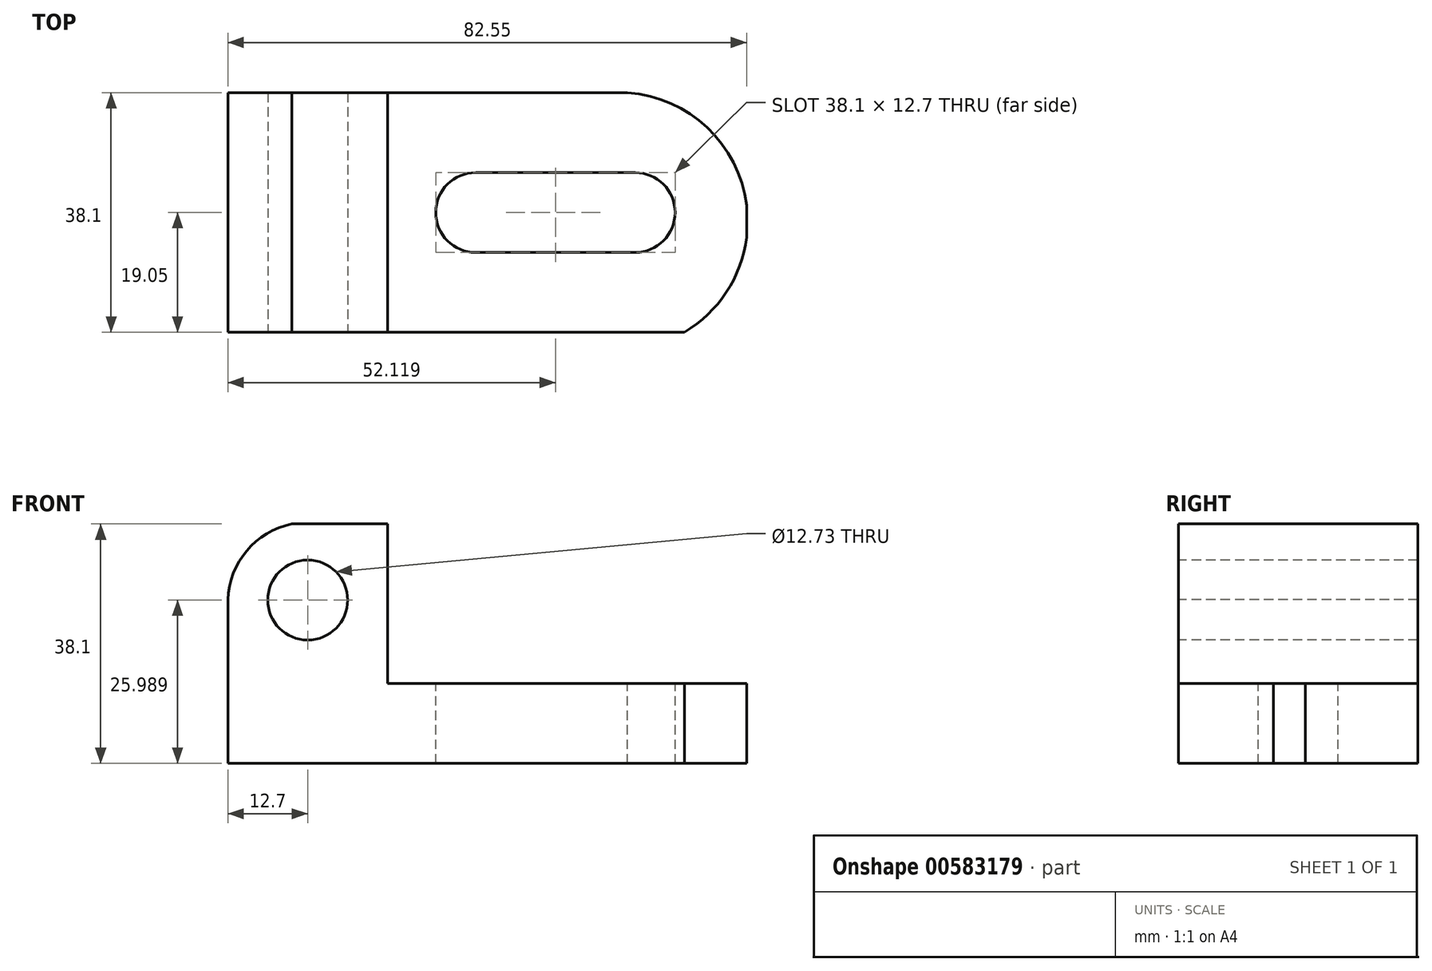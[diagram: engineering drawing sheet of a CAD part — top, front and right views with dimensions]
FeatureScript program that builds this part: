
annotation { "Feature Type Name" : "Feature", "Feature Type Description" : "" }
export const myFeature = defineFeature(function(context is Context, id is Id, definition is map)
    precondition{}
    {
        {
            var Q0;
            Q0=qCreatedBy(makeId("Front.planeOp"),FACE);
            var sketch = newSketch(context, id + "F0", { "sketchPlane" : qUnion([Q0])});
            skLineSegment(sketch, "E0.bottom", {"start": v(0, 0) * mm, "end": v(-82.55, 0) * mm});
            skLineSegment(sketch, "E0.top", {"start": v(0, 38.1) * mm, "end": v(-82.55, 38.1) * mm});
            skLineSegment(sketch, "E0.left", {"start": v(0, 0) * mm, "end": v(0, 38.1) * mm});
            skLineSegment(sketch, "E0.right", {"start": v(-82.55, 0) * mm, "end": v(-82.55, 38.1) * mm});
            skSolve(sketch);
        }
        {
            var Q0;
            Q0=makeQuery(id+"F0.imprint","IMPRINT",FACE,{"disambiguationData":[TD([[makeQuery(id+"F0.imprint","IMPRINT",EDGE,{"derivedFrom":sQuery(id+"F0.wireOp",EDGE,"E0.bottom")}),-1.0]])]});
            extrude(context, id + "F1", {"entities" : qUnion([Q0]), "depth" : 38.1 * mm, "offsetDistance" : 25.4 * mm});
        }
        {
            var Q0;
            Q0=makeQuery(id+"F1.opExtrude","CAP_FACE",FACE,{"disambiguationData":[OSD([sQuery(id+"F0.wireOp",EDGE,"E0.bottom"),sQuery(id+"F0.wireOp",EDGE,"E0.top"),sQuery(id+"F0.wireOp",EDGE,"E0.left"),sQuery(id+"F0.wireOp",EDGE,"E0.right")])],"isStart":false});
            var sketch = newSketch(context, id + "F2", { "sketchPlane" : qUnion([Q0])});
            skLineSegment(sketch, "E1", {"start": v(-57.15, 0) * mm, "end": v(-57.15, 12.7) * mm});
            skLineSegment(sketch, "E2", {"start": v(-57.15, 12.7) * mm, "end": v(-82.55, 12.7) * mm});
            skLineSegment(sketch, "E3", {"start": v(-57.15, 12.7) * mm, "end": v(-57.15, 38.1) * mm});
            skLineSegment(sketch, "E4", {"start": v(-57.15, 12.7) * mm, "end": v(0, 12.7) * mm});
            skSolve(sketch);
        }
        {
            var Q0;
            {var subQ0=sQuery(id+"F2.wireOp",EDGE,"E3");Q0=makeQuery(id+"F2.imprint","IMPRINT",FACE,{"disambiguationData":[TD([[makeQuery(id+"F2.imprint","IMPRINT",EDGE,{"derivedFrom":subQ0}),-1.0]])]});}
            extrude(context, id + "F3", {"entities" : qUnion([Q0]), "operationType" : NewBodyOperationType.REMOVE, "endBound" : BoundingType.THROUGH_ALL, "oppositeDirection" : true, "depth" : 25.4 * mm, "offsetDistance" : 25.4 * mm});
        }
        {
            var Q0;
            Q0=makeQuery(id+"F1.opExtrude","CAP_FACE",FACE,{"disambiguationData":[OSD([sQuery(id+"F0.wireOp",EDGE,"E0.bottom"),sQuery(id+"F0.wireOp",EDGE,"E0.top"),sQuery(id+"F0.wireOp",EDGE,"E0.left"),sQuery(id+"F0.wireOp",EDGE,"E0.right")])],"isStart":false});
            var sketch = newSketch(context, id + "F4", { "sketchPlane" : qUnion([Q0])});
            skCircle(sketch, "E5", {"center": v(-69.85, 25.99) * mm, "radius": 6.36 * mm});
            skSolve(sketch);
        }
        {
            var Q0;
            Q0=makeQuery(id+"F4.imprint","IMPRINT",FACE,{"disambiguationData":[TD([[makeQuery(id+"F4.imprint","IMPRINT",EDGE,{"derivedFrom":sQuery(id+"F4.wireOp",EDGE,"E5")}),1.0]])]});
            extrude(context, id + "F5", {"entities" : qUnion([Q0]), "operationType" : NewBodyOperationType.REMOVE, "endBound" : BoundingType.THROUGH_ALL, "oppositeDirection" : true, "depth" : 25.4 * mm, "offsetDistance" : 25.4 * mm});
        }
        {
            var Q0;
            Q0=makeQuery(id+"F3.boolean.opBoolean","COPY",FACE,{"derivedFrom":makeQuery(id+"F3.opExtrude","SWEPT_FACE",FACE,{"disambiguationData":[OSD([sQuery(id+"F2.wireOp",EDGE,"E4")])]})});
            var sketch = newSketch(context, id + "F6", { "sketchPlane" : qUnion([Q0])});
            skCircle(sketch, "E6", {"center": v(-43.13, -19.05) * mm, "radius": 6.35 * mm});
            skCircle(sketch, "E7", {"center": v(-17.73, -19.05) * mm, "radius": 6.35 * mm});
            skLineSegment(sketch, "E8", {"start": v(-43.13, -12.7) * mm, "end": v(-17.73, -12.7) * mm});
            skLineSegment(sketch, "E9", {"start": v(-43.13, -25.4) * mm, "end": v(-17.73, -25.4) * mm});
            skSolve(sketch);
        }
        {
            var Q0;
            {var subQ0=sQuery(id+"F6.wireOp",EDGE,"E8");Q0=makeQuery(id+"F6.imprint","IMPRINT",FACE,{"disambiguationData":[TD([[makeQuery(id+"F6.imprint","IMPRINT",EDGE,{"derivedFrom":subQ0}),-1.0]])]});}
            var Q1;
            {var subQ0=sQuery(id+"F6.wireOp",EDGE,"E6");var subQ1=makeQuery(id+"F6.imprint","INTERSECT",VERTEX,{"derivedFrom":[subQ0,sQuery(id+"F6.wireOp",EDGE,"E8")]});Q1=makeQuery(id+"F6.imprint","IMPRINT",FACE,{"disambiguationData":[TD([[makeQuery(id+"F6.imprint","IMPRINT",EDGE,{"disambiguationData":[TD([[subQ1,-1.0]])],"derivedFrom":subQ0}),1.0]])]});}
            var Q2;
            {var subQ0=sQuery(id+"F6.wireOp",EDGE,"E7");var subQ1=makeQuery(id+"F6.imprint","INTERSECT",VERTEX,{"derivedFrom":[subQ0,sQuery(id+"F6.wireOp",EDGE,"E8")]});Q2=makeQuery(id+"F6.imprint","IMPRINT",FACE,{"disambiguationData":[TD([[makeQuery(id+"F6.imprint","IMPRINT",EDGE,{"disambiguationData":[TD([[subQ1,-1.0]])],"derivedFrom":subQ0}),1.0]])]});}
            extrude(context, id + "F7", {"entities" : qUnion([Q0, Q1, Q2]), "operationType" : NewBodyOperationType.REMOVE, "oppositeDirection" : true, "depth" : 25.4 * mm, "offsetDistance" : 25.4 * mm});
        }
        {
            var Q0;
            Q0=makeQuery(id+"F1.opExtrude","CAP_FACE",FACE,{"disambiguationData":[OSD([sQuery(id+"F0.wireOp",EDGE,"E0.bottom"),sQuery(id+"F0.wireOp",EDGE,"E0.top"),sQuery(id+"F0.wireOp",EDGE,"E0.left"),sQuery(id+"F0.wireOp",EDGE,"E0.right")])],"isStart":false});
            var sketch = newSketch(context, id + "F8", { "sketchPlane" : qUnion([Q0])});
            skArc(sketch, "E10", {"start": v(-57.15, 25.4) * mm, "mid": v(-69.53, 38.35) * mm, "end": v(-82.55, 26.03) * mm});
            skSolve(sketch);
        }
        {
            var Q0;
            {var subQ0=sQuery(id+"F8.wireOp",EDGE,"E10");var subQ1=makeQuery(id+"F3.boolean.opBoolean","COPY",EDGE,{"derivedFrom":makeQuery(id+"F3.opExtrude","CAP_EDGE",EDGE,{"disambiguationData":[OSD([sQuery(id+"F2.wireOp",EDGE,"E3")])],"isStart":true})});var subQ2=makeQuery(id+"F8.imprint","INTERSECT",VERTEX,{"disambiguationData":[OD(1.0)],"derivedFrom":[subQ1,subQ0]});Q0=makeQuery(id+"F8.imprint","IMPRINT",FACE,{"disambiguationData":[TD([[makeQuery(id+"F8.imprint","IMPRINT",EDGE,{"disambiguationData":[TD([[subQ2,-1.0]])],"derivedFrom":subQ0}),-1.0]])]});}
            var Q1;
            {var subQ0=sQuery(id+"F8.wireOp",EDGE,"E10");var subQ1=makeQuery(id+"F1.opExtrude","CAP_EDGE",EDGE,{"disambiguationData":[OSD([sQuery(id+"F0.wireOp",EDGE,"E0.right")])],"isStart":false});var subQ2=makeQuery(id+"F8.imprint","INTERSECT",VERTEX,{"derivedFrom":[subQ1,subQ0]});Q1=makeQuery(id+"F8.imprint","IMPRINT",FACE,{"disambiguationData":[TD([[makeQuery(id+"F8.imprint","IMPRINT",EDGE,{"disambiguationData":[TD([[subQ2,1.0]])],"derivedFrom":subQ0}),-1.0]])]});}
            extrude(context, id + "F9", {"entities" : qUnion([Q0, Q1]), "operationType" : NewBodyOperationType.ADD, "depth" : 25.4 * mm, "offsetDistance" : 25.4 * mm});
        }
        {
            var Q0;
            Q0=makeQuery(id+"F9.opExtrude","CAP_FACE",FACE,{"disambiguationData":[OSD([sQuery(id+"F0.wireOp",EDGE,"E0.top"),sQuery(id+"F2.wireOp",EDGE,"E3"),sQuery(id+"F8.wireOp",EDGE,"E10")])],"isStart":false});
            var Q1;
            Q1=makeQuery(id+"F9.opExtrude","CAP_FACE",FACE,{"disambiguationData":[OSD([sQuery(id+"F0.wireOp",EDGE,"E0.top"),sQuery(id+"F0.wireOp",EDGE,"E0.right"),sQuery(id+"F8.wireOp",EDGE,"E10")])],"isStart":false});
            extrude(context, id + "F10", {"entities" : qUnion([Q0, Q1]), "operationType" : NewBodyOperationType.REMOVE, "endBound" : BoundingType.THROUGH_ALL, "oppositeDirection" : true, "depth" : 25.4 * mm, "offsetDistance" : 25.4 * mm});
        }
        {
            var Q0;
            Q0=makeQuery(id+"F3.boolean.opBoolean","COPY",FACE,{"derivedFrom":makeQuery(id+"F3.opExtrude","SWEPT_FACE",FACE,{"disambiguationData":[OSD([sQuery(id+"F2.wireOp",EDGE,"E4")])]})});
            var sketch = newSketch(context, id + "F11", { "sketchPlane" : qUnion([Q0])});
            skArc(sketch, "E11", {"start": v(-9.9, -38.1) * mm, "mid": v(-0.4, -15.72) * mm, "end": v(-18.96, 0) * mm});
            skSolve(sketch);
        }
        {
            var Q0;
            Q0 = qSketchRegion(id + "F11", true);
            var Q1;
            {var subQ0=sQuery(id+"F11.wireOp",EDGE,"E11");var subQ1=sQuery(id+"F2.wireOp",EDGE,"E4");var subQ2=sQuery(id+"F0.wireOp",EDGE,"E0.left");var subQ5=makeQuery(id+"F3.boolean.opBoolean","COPY",EDGE,{"derivedFrom":makeQuery(id+"F3.opExtrude","SWEPT_EDGE",EDGE,{"disambiguationData":[OSD([subQ2,subQ1])]})});var subQ6=makeQuery(id+"F11.imprint","INTERSECT",VERTEX,{"disambiguationData":[OD(1.0)],"derivedFrom":[subQ5,subQ0]});Q1=makeQuery(id+"F11.imprint","IMPRINT",FACE,{"disambiguationData":[TD([[makeQuery(id+"F11.imprint","IMPRINT",EDGE,{"disambiguationData":[TD([[subQ6,-1.0]])],"derivedFrom":subQ0}),-1.0]])]});}
            var Q2;
            {var subQ0=sQuery(id+"F11.wireOp",EDGE,"E11");var subQ1=sQuery(id+"F2.wireOp",EDGE,"E4");var subQ2=makeQuery(id+"F3.boolean.opBoolean","COPY",EDGE,{"derivedFrom":makeQuery(id+"F3.opExtrude","CAP_EDGE",EDGE,{"disambiguationData":[OSD([subQ1])],"isStart":true})});var subQ3=makeQuery(id+"F11.imprint","INTERSECT",VERTEX,{"derivedFrom":[subQ2,subQ0]});Q2=makeQuery(id+"F11.imprint","IMPRINT",FACE,{"disambiguationData":[TD([[makeQuery(id+"F11.imprint","IMPRINT",EDGE,{"disambiguationData":[TD([[subQ3,-1.0]])],"derivedFrom":subQ0}),-1.0]])]});}
            extrude(context, id + "F12", {"entities" : qUnion([Q0, Q1, Q2]), "operationType" : NewBodyOperationType.REMOVE, "oppositeDirection" : true, "depth" : 25.4 * mm, "offsetDistance" : 25.4 * mm});
        }
    });
